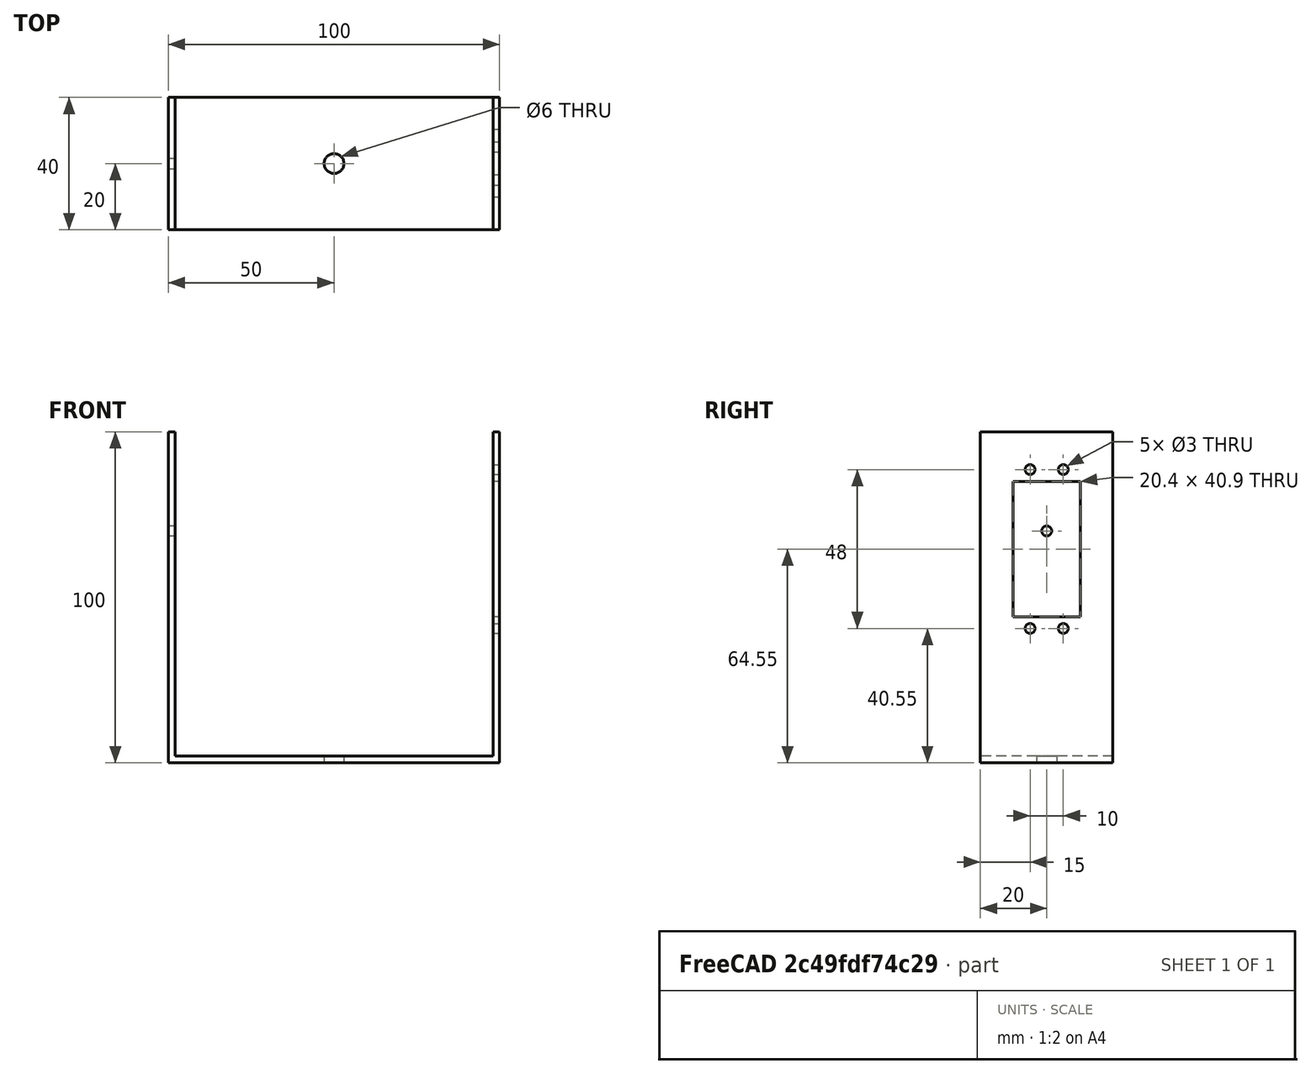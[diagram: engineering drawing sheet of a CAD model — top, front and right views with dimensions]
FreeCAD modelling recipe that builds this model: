
FCSTD DOCUMENT  (FreeCAD 0.20R29410 (Git))
Label: camera_stand
License: All rights reserved
LicenseURL: http://en.wikipedia.org/wiki/All_rights_reserved
objects: Sketcher::SketchObject×5, PartDesign::Pocket×3, PartDesign::Pad×1, PartDesign::Hole×1, PartDesign::Fillet×1, PartDesign::Body×1, Mesh::Feature×1
note: 18 computed .brp shape members not serialized (recipe doc carries the construction recipe); baked Part::Feature solids carry a one-line shape summary decoded from their .brp

FEATURE [Sketcher::SketchObject] Sketch
  FullyConstrained = true
  MapMode = 5
  Support = -> [XY_Plane]
  sketch-geometry (4):
    g0: LineSegment StartX=-50 StartY=-20 StartZ=0 EndX=50 EndY=-20 EndZ=0
    g1: LineSegment StartX=50 StartY=-20 StartZ=0 EndX=50 EndY=20 EndZ=0
    g2: LineSegment StartX=50 StartY=20 StartZ=0 EndX=-50 EndY=20 EndZ=0
    g3: LineSegment StartX=-50 StartY=20 StartZ=0 EndX=-50 EndY=-20 EndZ=0
  constraints (10):
    c: Coincident(g0,g1)
    c: Coincident(g1,g2)
    c: Coincident(g2,g3)
    c: Coincident(g3,g0)
    c: Horizontal(g0)
    c: Vertical(g1)
    c: Symmetric(g2,g1,g-2)
    c: Symmetric(g0,g2,g-1)
    c: Distance(g2) = 100
    c: Distance(g1) = 40
FEATURE [PartDesign::Pad] Pad
  Direction = (0,0,1)
  Length = 100
  Length2 = 10
  Profile = -> Sketch
  ReferenceAxis = -> Sketch [N_Axis]
  Type = 0
FEATURE [Sketcher::SketchObject] Sketch001
  FullyConstrained = true
  MapMode = 5
  Placement = pos=(0,0,100) rot=(0,0,1;0rad)
  Support = -> [Pad]
  sketch-geometry (4):
    g0: LineSegment StartX=-48 StartY=20 StartZ=0 EndX=48 EndY=20 EndZ=0
    g1: LineSegment StartX=48 StartY=20 StartZ=0 EndX=48 EndY=-20 EndZ=0
    g2: LineSegment StartX=48 StartY=-20 StartZ=0 EndX=-48 EndY=-20 EndZ=0
    g3: LineSegment StartX=-48 StartY=-20 StartZ=0 EndX=-48 EndY=20 EndZ=0
  constraints (10):
    c: Coincident(g0,g1)
    c: Coincident(g1,g2)
    c: Coincident(g2,g3)
    c: Coincident(g3,g0)
    c: Horizontal(g2)
    c: Vertical(g1)
    c: Symmetric(g0,g0,g-2)
    c: Symmetric(g0,g2,g-1)
    c: Distance(g0) = 96
    c: Distance(g1) = 40
FEATURE [PartDesign::Pocket] Pocket
  BaseFeature = -> Pad
  Direction = (0,0,-1)
  Length = 98
  Length2 = 5
  Profile = -> Sketch001
  ReferenceAxis = -> Sketch001 [N_Axis]
  Type = 0
FEATURE [Sketcher::SketchObject] Sketch002
  FullyConstrained = true
  MapMode = 5
  Placement = pos=(0,0,2) rot=(0,0,1;0rad)
  Support = -> [Pocket]
  sketch-geometry (1):
    g0: Circle CenterX=0 CenterY=0 CenterZ=0 NormalX=0 NormalY=0 NormalZ=1 AngleXU=0 Radius=3.5
  constraints (2):
    c: Coincident(g0,g-1)
    c: Diameter(g0) = 7
FEATURE [PartDesign::Hole] Hole
  BaseFeature = -> Pocket
  CustomThreadClearance = 0
  Depth = 25
  DepthType = 0
  Diameter = 6
  DrillForDepth = false
  DrillPoint = 1
  DrillPointAngle = 118
  HoleCutCountersinkAngle = 90
  HoleCutCustomValues = false
  HoleCutDepth = 0
  HoleCutDiameter = 6.1
  HoleCutType = 0
  ModelThread = false
  Profile = -> Sketch002
  Tapered = false
  TaperedAngle = 90
  ThreadClass = 0
  ThreadDepth = 25
  ThreadDepthType = 0
  ThreadDirection = 0
  ThreadFit = 0
  ThreadSize = 0
  ThreadType = 0
  Threaded = false
  UseCustomThreadClearance = false
FEATURE [Sketcher::SketchObject] Sketch003
  FullyConstrained = true
  MapMode = 5
  Placement = pos=(50,0,0) rot=(0.57735,0.57735,0.57735;2.0944rad)
  Support = -> [Hole]
  sketch-geometry (9):
    g0: LineSegment StartX=-10.2 StartY=85 StartZ=0 EndX=10.2 EndY=85 EndZ=0
    g1: LineSegment StartX=10.2 StartY=85 StartZ=0 EndX=10.2 EndY=44.1 EndZ=0
    g2: LineSegment StartX=10.2 StartY=44.1 StartZ=0 EndX=-10.2 EndY=44.1 EndZ=0
    g3: LineSegment StartX=-10.2 StartY=44.1 StartZ=0 EndX=-10.2 EndY=85 EndZ=0
    g4: Circle CenterX=-5 CenterY=88.55 CenterZ=0 NormalX=0 NormalY=0 NormalZ=1 AngleXU=0 Radius=1.5
    g5: Circle CenterX=5 CenterY=88.55 CenterZ=0 NormalX=0 NormalY=0 NormalZ=1 AngleXU=0 Radius=1.5
    g6: Circle CenterX=-5 CenterY=40.55 CenterZ=0 NormalX=0 NormalY=0 NormalZ=1 AngleXU=0 Radius=1.5
    g7: Circle CenterX=5 CenterY=40.55 CenterZ=0 NormalX=0 NormalY=0 NormalZ=1 AngleXU=0 Radius=1.5
    g8: GeomPoint X=-8e-16 Y=64.55 Z=0
  constraints (21):
    c: Coincident(g0,g1)
    c: Coincident(g1,g2)
    c: Coincident(g2,g3)
    c: Coincident(g3,g0)
    c: Horizontal(g2)
    c: Vertical(g1)
    c: Vertical(g3)
    c: Distance(g1) = 40.9
    c: Distance(g0) = 20.4
    c: Symmetric(g0,g0,g-2)
    c: DistanceY(g-1,g0) = 85
    c: Symmetric(g4,g5,g-2)
    c: Symmetric(g6,g7,g-2)
    c: Diameter(g4) = 3
    c: Diameter(g5) = 3
    c: Diameter(g6) = 3
    c: Diameter(g7) = 3
    c: Distance(g6,g4) = 48
    c: Symmetric(g2,g0,g8)
    c: Symmetric(g7,g4,g8)
    c: Distance(g4,g5) = 10
FEATURE [PartDesign::Pocket] Pocket001
  BaseFeature = -> Hole
  Direction = (-1,0,0)
  Length = 2
  Length2 = 5
  Profile = -> Sketch003
  ReferenceAxis = -> Sketch003 [N_Axis]
  Type = 0
FEATURE [Sketcher::SketchObject] Sketch004
  FullyConstrained = true
  MapMode = 5
  Placement = pos=(-50,0,0) rot=(0.57735,-0.57735,-0.57735;2.0944rad)
  Support = -> [Pocket001]
  sketch-geometry (1):
    g0: Circle CenterX=0 CenterY=70 CenterZ=0 NormalX=0 NormalY=0 NormalZ=1 AngleXU=0 Radius=1.5
  constraints (3):
    c: PointOnObject(g0,g-2)
    c: DistanceY(g-1,g0) = 70
    c: Diameter(g0) = 3
FEATURE [PartDesign::Pocket] Pocket002
  BaseFeature = -> Pocket001
  Direction = (1,0,0)
  Length = 2
  Length2 = 5
  Profile = -> Sketch004
  ReferenceAxis = -> Sketch004 [N_Axis]
  Type = 0
FEATURE [PartDesign::Fillet] Fillet
  Base = -> Pocket002 [Face1,Face9,Face8]
  BaseFeature = -> Pocket002
  Radius = 1
  SupportTransform = false
  UseAllEdges = false
FEATURE [PartDesign::Body] Body
  Group = -> [Sketch,Pad,Sketch001,Pocket,Sketch002,Hole,Sketch003,Pocket001,Sketch004,Pocket002,Fillet]
  Origin = -> Origin
  Tip = -> Fillet
FEATURE [Mesh::Feature] Mesh  label="Body (Meshed)"
